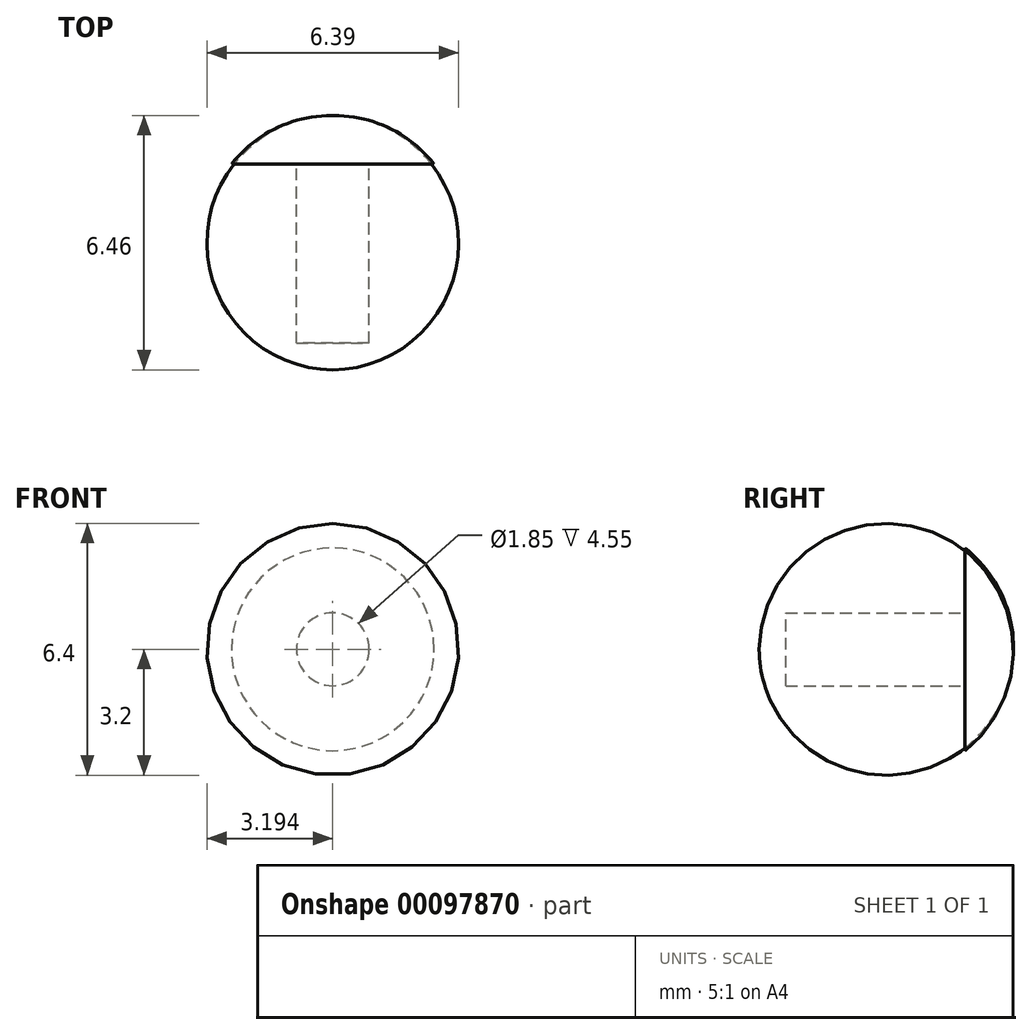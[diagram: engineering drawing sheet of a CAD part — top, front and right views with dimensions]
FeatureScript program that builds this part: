
annotation { "Feature Type Name" : "Feature", "Feature Type Description" : "" }
export const myFeature = defineFeature(function(context is Context, id is Id, definition is map)
    precondition{}
    {
        {
            var Q0;
            Q0=qCreatedBy(makeId("Top.planeOp"),FACE);
            var sketch = newSketch(context, id + "F0", { "sketchPlane" : qUnion([Q0])});
            skLineSegment(sketch, "E0", {"start": v(-27.14, 10.6) * mm, "end": v(-27.14, 13.08) * mm});
            skLineSegment(sketch, "E1", {"start": v(-27.14, 10.6) * mm, "end": v(-24.56, 10.6) * mm});
            skArc(sketch, "E2", {"start": v(-24.56, 10.6) * mm, "mid": v(-25.7, 11.53) * mm, "end": v(-27.14, 11.84) * mm});
            skSolve(sketch);
        }
        {
            var Q0;
            Q0 = qSketchRegion(id + "F0", true);
            var Q1;
            Q1=sQuery(id+"F0.wireOp",EDGE,"E0");
            revolve(context, id + "F1", {"entities" : qUnion([Q0]), "axis" : qUnion([Q1]), "revolveType" : RevolveType.FULL});
        }
        {
            var Q0;
            Q0=makeQuery(id+"F1.opRevolve","SWEPT_FACE",FACE,{"disambiguationData":[OSD([sQuery(id+"F0.wireOp",EDGE,"E1")])]});
            var sketch = newSketch(context, id + "F2", { "sketchPlane" : qUnion([Q0])});
            skPoint(sketch, "E3", {"position": v(-27.14, 0) * mm});
            skCircle(sketch, "E4", {"center": v(-27.14, 0) * mm, "radius": 0.93 * mm});
            skSolve(sketch);
        }
        {
            var Q0;
            Q0 = qSketchRegion(id + "F2", true);
            extrude(context, id + "F3", {"entities" : qUnion([Q0]), "operationType" : NewBodyOperationType.ADD, "depth" : 4.55 * mm});
        }
    });
